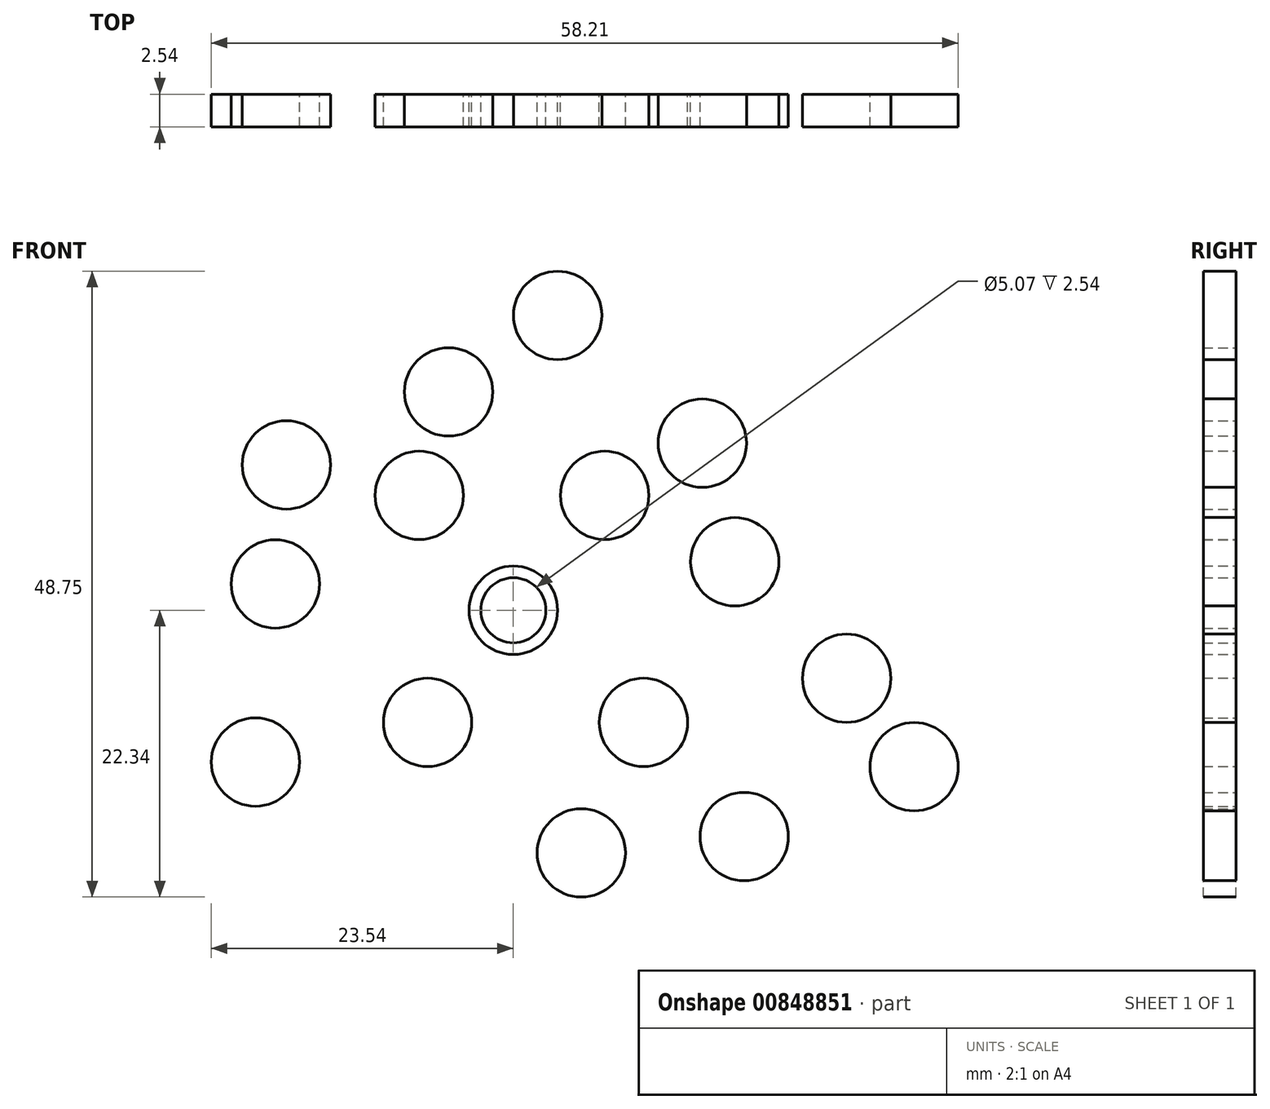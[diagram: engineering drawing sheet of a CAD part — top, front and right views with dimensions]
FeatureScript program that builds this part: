
annotation { "Feature Type Name" : "Feature", "Feature Type Description" : "" }
export const myFeature = defineFeature(function(context is Context, id is Id, definition is map)
    precondition{}
    {
        {
            var Q0;
            Q0=qCreatedBy(makeId("Front.planeOp"),FACE);
            var sketch = newSketch(context, id + "F0", { "sketchPlane" : qUnion([Q0])});
            skCircle(sketch, "E0", {"center": v(0, 0) * mm, "radius": 3.45 * mm});
            skSolve(sketch);
        }
        {
            var Q0;
            Q0=qSketchRegion(id+"F0",true);
            extrude(context, id + "F1", {"entities" : qUnion([Q0]), "depth" : 2.54 * mm});
        }
        {
            var Q0;
            Q0=qCreatedBy(makeId("Front.planeOp"),FACE);
            var sketch = newSketch(context, id + "F2", { "sketchPlane" : qUnion([Q0])});
            skCircle(sketch, "E1", {"center": v(0, 0) * mm, "radius": 2.53 * mm});
            skSolve(sketch);
        }
        {
            var Q0;
            Q0=makeQuery(id+"F2.imprint","IMPRINT",FACE,{"disambiguationData":[TD([[makeQuery(id+"F2.imprint","IMPRINT",EDGE,{"derivedFrom":sQuery(id+"F2.wireOp",EDGE,"E1")}),1.0]])]});
            extrude(context, id + "F3", {"entities" : qUnion([Q0]), "operationType" : NewBodyOperationType.REMOVE, "depth" : 25.15 * mm});
        }
        {
            var Q0;
            Q0=qCreatedBy(makeId("Front.planeOp"),FACE);
            var sketch = newSketch(context, id + "F4", { "sketchPlane" : qUnion([Q0])});
            skCircle(sketch, "E2", {"center": v(-18.55, 2.05) * mm, "radius": 3.44 * mm});
            skCircle(sketch, "E3", {"center": v(17.25, 3.77) * mm, "radius": 3.44 * mm});
            skCircle(sketch, "E4", {"center": v(7.12, 8.95) * mm, "radius": 3.44 * mm});
            skCircle(sketch, "E5", {"center": v(-7.33, 8.95) * mm, "radius": 3.44 * mm});
            skCircle(sketch, "E6", {"center": v(10.14, -8.73) * mm, "radius": 3.44 * mm});
            skCircle(sketch, "E7", {"center": v(-6.69, -8.73) * mm, "radius": 3.44 * mm});
            skSolve(sketch);
        }
        {
            var Q0;
            Q0 = qSketchRegion(id + "F4", true);
            extrude(context, id + "F5", {"entities" : qUnion([Q0]), "depth" : 2.54 * mm, "offsetDistance" : 25.4 * mm});
        }
        {
            var Q0;
            Q0=qCreatedBy(makeId("Front.planeOp"),FACE);
            var sketch = newSketch(context, id + "F6", { "sketchPlane" : qUnion([Q0])});
            skCircle(sketch, "E8", {"center": v(-17.68, 11.32) * mm, "radius": 3.44 * mm});
            skCircle(sketch, "E9", {"center": v(3.45, 22.97) * mm, "radius": 3.44 * mm});
            skCircle(sketch, "E10", {"center": v(-5.04, 17) * mm, "radius": 3.44 * mm});
            skCircle(sketch, "E11", {"center": v(14.72, 13.02) * mm, "radius": 3.44 * mm});
            skCircle(sketch, "E12", {"center": v(-20.1, -11.83) * mm, "radius": 3.44 * mm});
            skCircle(sketch, "E13", {"center": v(31.23, -12.19) * mm, "radius": 3.44 * mm});
            skCircle(sketch, "E14", {"center": v(25.97, -5.3) * mm, "radius": 3.44 * mm});
            skCircle(sketch, "E15", {"center": v(17.99, -17.63) * mm, "radius": 3.44 * mm});
            skCircle(sketch, "E16", {"center": v(5.3, -18.9) * mm, "radius": 3.44 * mm});
            skSolve(sketch);
        }
        {
            var Q0;
            Q0=makeQuery(id+"F6.imprint","IMPRINT",FACE,{"disambiguationData":[TD([[makeQuery(id+"F6.imprint","IMPRINT",EDGE,{"derivedFrom":sQuery(id+"F6.wireOp",EDGE,"E8")}),1.0]])]});
            var Q1;
            Q1=makeQuery(id+"F6.imprint","IMPRINT",FACE,{"disambiguationData":[TD([[makeQuery(id+"F6.imprint","IMPRINT",EDGE,{"derivedFrom":sQuery(id+"F6.wireOp",EDGE,"E10")}),1.0]])]});
            var Q2;
            Q2=makeQuery(id+"F6.imprint","IMPRINT",FACE,{"disambiguationData":[TD([[makeQuery(id+"F6.imprint","IMPRINT",EDGE,{"derivedFrom":sQuery(id+"F6.wireOp",EDGE,"E9")}),1.0]])]});
            var Q3;
            Q3=makeQuery(id+"F6.imprint","IMPRINT",FACE,{"disambiguationData":[TD([[makeQuery(id+"F6.imprint","IMPRINT",EDGE,{"derivedFrom":sQuery(id+"F6.wireOp",EDGE,"E11")}),1.0]])]});
            var Q4;
            Q4=makeQuery(id+"F6.imprint","IMPRINT",FACE,{"disambiguationData":[TD([[makeQuery(id+"F6.imprint","IMPRINT",EDGE,{"derivedFrom":sQuery(id+"F6.wireOp",EDGE,"E14")}),1.0]])]});
            var Q5;
            Q5=makeQuery(id+"F6.imprint","IMPRINT",FACE,{"disambiguationData":[TD([[makeQuery(id+"F6.imprint","IMPRINT",EDGE,{"derivedFrom":sQuery(id+"F6.wireOp",EDGE,"E13")}),1.0]])]});
            var Q6;
            Q6=makeQuery(id+"F6.imprint","IMPRINT",FACE,{"disambiguationData":[TD([[makeQuery(id+"F6.imprint","IMPRINT",EDGE,{"derivedFrom":sQuery(id+"F6.wireOp",EDGE,"E15")}),1.0]])]});
            var Q7;
            Q7=makeQuery(id+"F6.imprint","IMPRINT",FACE,{"disambiguationData":[TD([[makeQuery(id+"F6.imprint","IMPRINT",EDGE,{"derivedFrom":sQuery(id+"F6.wireOp",EDGE,"E16")}),1.0]])]});
            var Q8;
            Q8=makeQuery(id+"F6.imprint","IMPRINT",FACE,{"disambiguationData":[TD([[makeQuery(id+"F6.imprint","IMPRINT",EDGE,{"derivedFrom":sQuery(id+"F6.wireOp",EDGE,"E12")}),1.0]])]});
            extrude(context, id + "F7", {"entities" : qUnion([Q0, Q1, Q2, Q3, Q4, Q5, Q6, Q7, Q8]), "depth" : 2.54 * mm, "offsetDistance" : 25.4 * mm});
        }
    });
